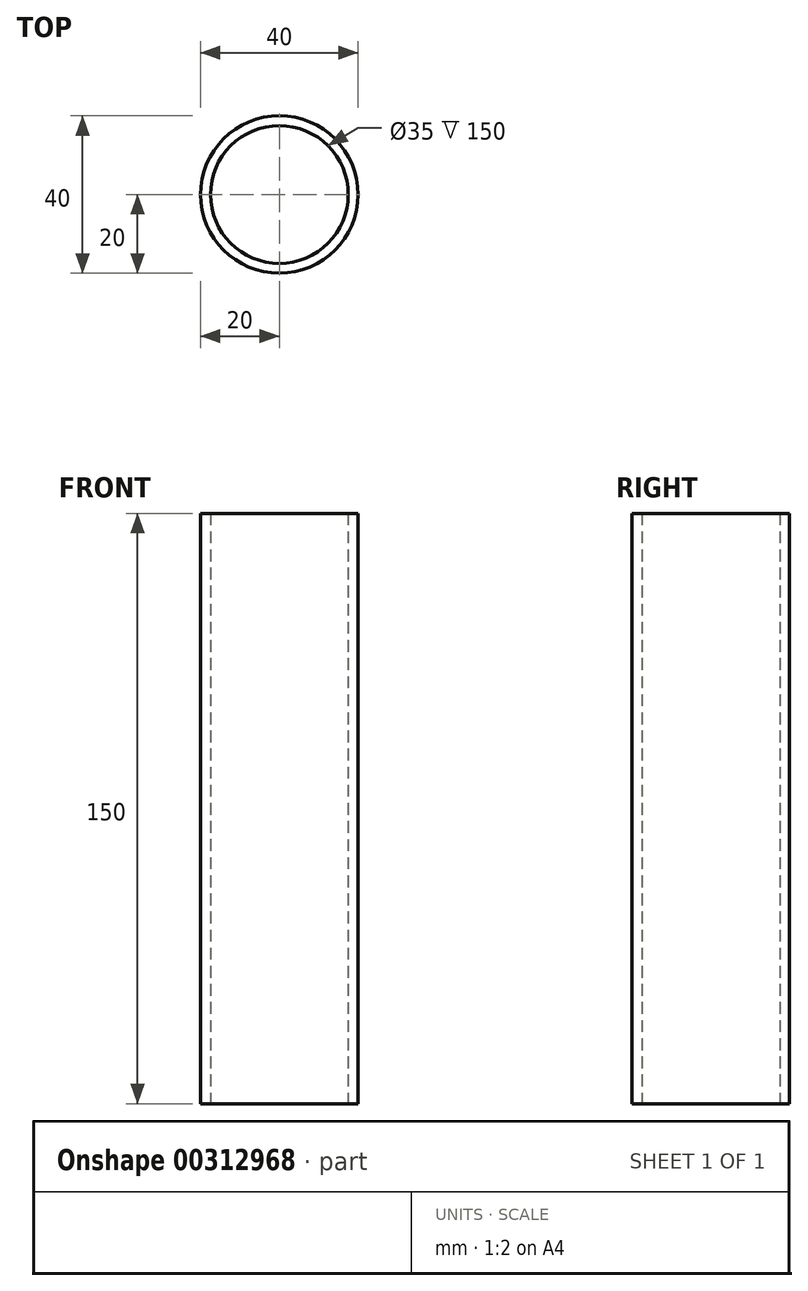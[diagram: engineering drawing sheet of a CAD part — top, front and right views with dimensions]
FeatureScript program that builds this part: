
annotation { "Feature Type Name" : "Feature", "Feature Type Description" : "" }
export const myFeature = defineFeature(function(context is Context, id is Id, definition is map)
    precondition{}
    {
        {
            var Q0;
            Q0=qCreatedBy(makeId("Top.planeOp"),FACE);
            var sketch = newSketch(context, id + "F0", { "sketchPlane" : qUnion([Q0])});
            skCircle(sketch, "E0", {"center": v(0, 0) * mm, "radius": 20 * mm});
            skCircle(sketch, "E1", {"center": v(0, 0) * mm, "radius": 17.5 * mm});
            skSolve(sketch);
        }
        {
            var Q0;
            Q0=makeQuery(id+"F0.imprint","IMPRINT",FACE,{"disambiguationData":[TD([[makeQuery(id+"F0.imprint","IMPRINT",EDGE,{"derivedFrom":sQuery(id+"F0.wireOp",EDGE,"E0")}),1.0]])]});
            extrude(context, id + "F1", {"entities" : qUnion([Q0]), "depth" : 150 * mm});
        }
    });
